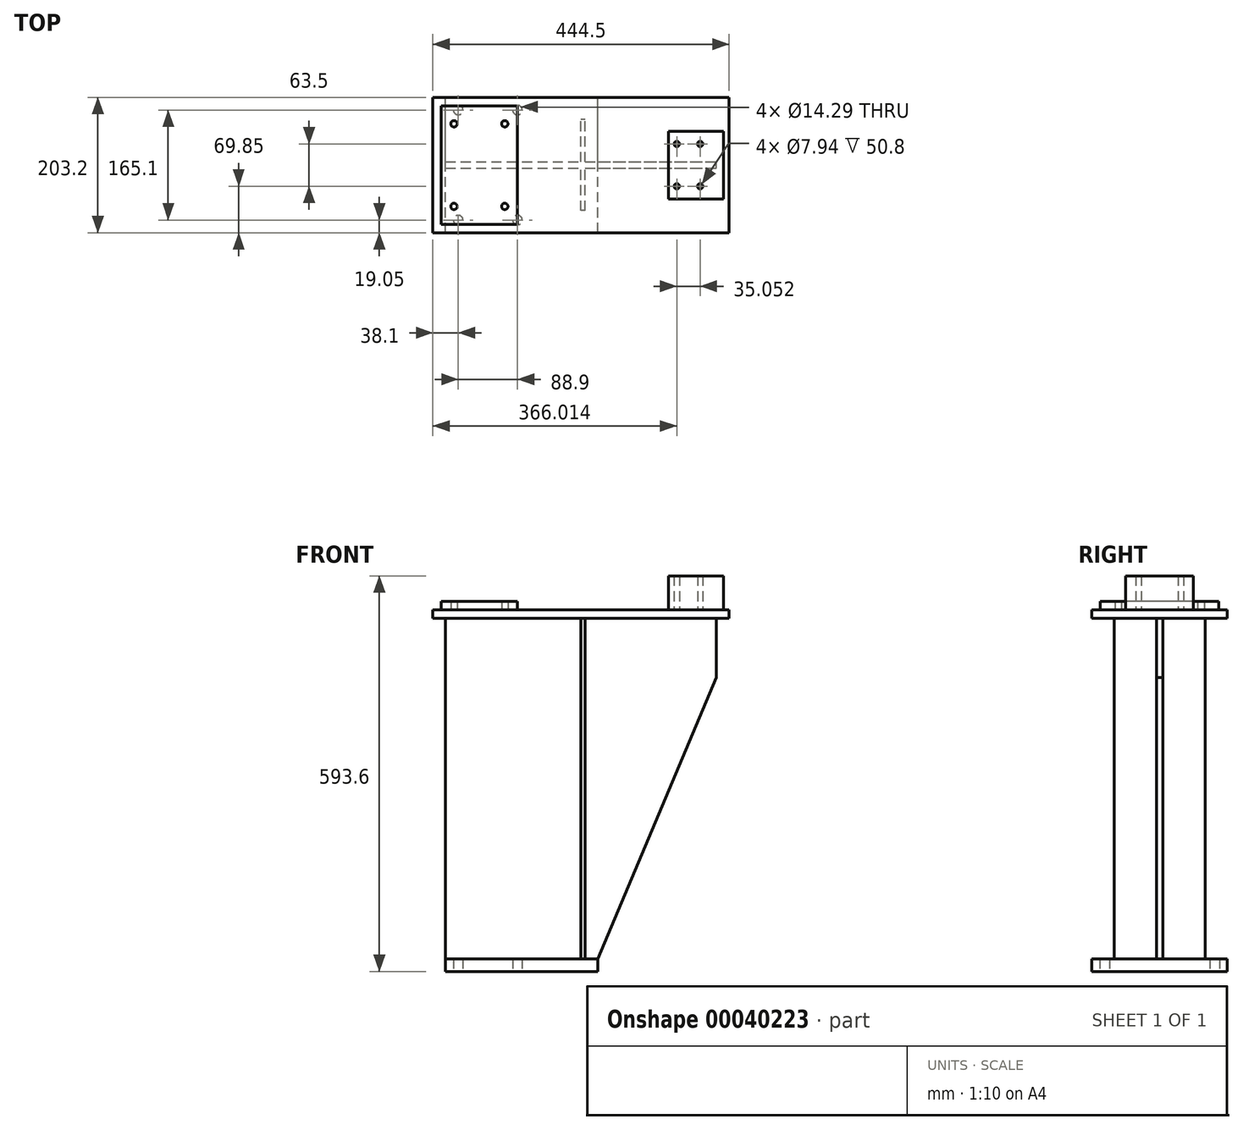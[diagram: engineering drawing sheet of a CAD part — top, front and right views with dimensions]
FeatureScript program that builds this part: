
annotation { "Feature Type Name" : "Feature", "Feature Type Description" : "" }
export const myFeature = defineFeature(function(context is Context, id is Id, definition is map)
    precondition{}
    {
        {
            var Q0;
            Q0=qCreatedBy(makeId("Top.planeOp"),FACE);
            var sketch = newSketch(context, id + "F0", { "sketchPlane" : qUnion([Q0])});
            skLineSegment(sketch, "E0.rect.bottom", {"start": v(-222.25, 101.6) * mm, "end": v(222.25, 101.6) * mm});
            skLineSegment(sketch, "E0.rect.top", {"start": v(-222.25, -101.6) * mm, "end": v(222.25, -101.6) * mm});
            skLineSegment(sketch, "E0.rect.left", {"start": v(-222.25, 101.6) * mm, "end": v(-222.25, -101.6) * mm});
            skLineSegment(sketch, "E0.rect.right", {"start": v(222.25, 101.6) * mm, "end": v(222.25, -101.6) * mm});
            skPoint(sketch, "E0.rect.middle", {"position": v(0, 0) * mm});
            skSolve(sketch);
        }
        {
            var Q0;
            Q0 = qSketchRegion(id + "F0", true);
            extrude(context, id + "F1", {"entities" : qUnion([Q0]), "oppositeDirection" : true, "depth" : 12.7 * mm});
        }
        {
            var Q0;
            Q0=qCreatedBy(makeId("Front.planeOp"),FACE);
            var sketch = newSketch(context, id + "F2", { "sketchPlane" : qUnion([Q0])});
            skLineSegment(sketch, "E1.0", {"start": v(-222.25, -12.7) * mm, "end": v(222.25, -12.7) * mm, "construction": true});
            skLineSegment(sketch, "E2", {"start": v(0, -12.7) * mm, "end": v(0, -523.75) * mm, "construction": true});
            skPoint(sketch, "E2.endSnap0", {"position": v(0, -12.7) * mm});
            skLineSegment(sketch, "E3.0", {"start": v(-203.2, -12.7) * mm, "end": v(-203.2, -523.75) * mm});
            skLineSegment(sketch, "E4.0", {"start": v(203.2, -12.7) * mm, "end": v(203.2, -101.6) * mm});
            skLineSegment(sketch, "E5", {"start": v(-203.2, -523.75) * mm, "end": v(25.4, -523.75) * mm});
            skLineSegment(sketch, "E6", {"start": v(203.2, -12.7) * mm, "end": v(-203.2, -12.7) * mm, "construction": true});
            skLineSegment(sketch, "E7.0", {"start": v(25.4, -12.7) * mm, "end": v(25.4, -523.75) * mm, "construction": true});
            skLineSegment(sketch, "E8.0", {"start": v(203.2, -101.6) * mm, "end": v(-203.2, -101.6) * mm, "construction": true});
            skLineSegment(sketch, "E9", {"start": v(25.4, -523.75) * mm, "end": v(203.2, -101.6) * mm});
            skLineSegment(sketch, "E10", {"start": v(-203.2, -12.7) * mm, "end": v(203.2, -12.7) * mm});
            skSolve(sketch);
        }
        {
            var Q0;
            Q0 = qSketchRegion(id + "F2", true);
            extrude(context, id + "F3", {"entities" : qUnion([Q0]), "operationType" : NewBodyOperationType.ADD, "endBound" : BoundingType.SYMMETRIC, "depth" : 9.65 * mm});
        }
        {
            var Q0;
            Q0=qCreatedBy(makeId("Front.planeOp"),FACE);
            var sketch = newSketch(context, id + "F4", { "sketchPlane" : qUnion([Q0])});
            skLineSegment(sketch, "E11", {"start": v(0, 171.52) * mm, "end": v(0, -557.34) * mm, "construction": true});
            skLineSegment(sketch, "E12.0", {"start": v(0, -12.7) * mm, "end": v(0, -523.75) * mm});
            skLineSegment(sketch, "E13.0", {"start": v(6.35, -12.7) * mm, "end": v(6.35, -523.75) * mm});
            skLineSegment(sketch, "E14", {"start": v(6.35, -12.7) * mm, "end": v(0, -12.7) * mm});
            skLineSegment(sketch, "E15", {"start": v(0, -523.75) * mm, "end": v(6.35, -523.75) * mm});
            skSolve(sketch);
        }
        {
            var Q0;
            Q0 = qSketchRegion(id + "F4", true);
            extrude(context, id + "F5", {"entities" : qUnion([Q0]), "operationType" : NewBodyOperationType.ADD, "endBound" : BoundingType.SYMMETRIC, "depth" : 136.53 * mm});
        }
        {
            var Q0;
            Q0=makeQuery(id+"F5.boolean.opBoolean","MERGE",FACE,{"derivedFrom":[makeQuery(id+"F3.opExtrude","SWEPT_FACE",FACE,{"disambiguationData":[OSD([sQuery(id+"F2.wireOp",EDGE,"E5")])]}),makeQuery(id+"F5.opExtrude","SWEPT_FACE",FACE,{"disambiguationData":[OSD([sQuery(id+"F4.wireOp",EDGE,"E15")])]})]});
            var sketch = newSketch(context, id + "F6", { "sketchPlane" : qUnion([Q0])});
            skLineSegment(sketch, "E16.0", {"start": v(-203.2, 101.6) * mm, "end": v(-203.2, -4.83) * mm});
            skLineSegment(sketch, "E17", {"start": v(0, 0) * mm, "end": v(-240.16, 0) * mm, "construction": true});
            skLineSegment(sketch, "E18.0", {"start": v(25.4, 101.6) * mm, "end": v(-203.2, 101.6) * mm});
            skPoint(sketch, "E19.orphan", {"position": v(-203.2, 4.83) * mm});
            skLineSegment(sketch, "E20.0", {"start": v(25.4, 101.6) * mm, "end": v(25.4, -4.83) * mm});
            skLineSegment(sketch, "E21.MirrorCS", {"start": v(-203.2, -101.6) * mm, "end": v(-203.2, 4.83) * mm});
            skLineSegment(sketch, "E22.MirrorCS", {"start": v(25.4, -101.6) * mm, "end": v(-203.2, -101.6) * mm});
            skLineSegment(sketch, "E23.MirrorCS", {"start": v(25.4, -101.6) * mm, "end": v(25.4, 4.83) * mm});
            skSolve(sketch);
        }
        {
            var Q0;
            Q0 = qSketchRegion(id + "F6", true);
            extrude(context, id + "F7", {"entities" : qUnion([Q0]), "operationType" : NewBodyOperationType.ADD, "depth" : 19.05 * mm});
        }
        {
            var Q0;
            Q0=makeQuery(id+"F7.opExtrude","CAP_FACE",FACE,{"disambiguationData":[OSD([sQuery(id+"F6.wireOp",EDGE,"E16.0"),sQuery(id+"F6.wireOp",EDGE,"E18.0"),sQuery(id+"F6.wireOp",EDGE,"E20.0"),sQuery(id+"F6.wireOp",EDGE,"E21.MirrorCS"),sQuery(id+"F6.wireOp",EDGE,"E22.MirrorCS"),sQuery(id+"F6.wireOp",EDGE,"E23.MirrorCS")])],"isStart":false});
            var sketch = newSketch(context, id + "F8", { "sketchPlane" : qUnion([Q0])});
            skLineSegment(sketch, "E24.0", {"start": v(-184.15, 101.6) * mm, "end": v(-184.15, -101.6) * mm, "construction": true});
            skLineSegment(sketch, "E25.0", {"start": v(-95.25, 101.6) * mm, "end": v(-95.25, -101.6) * mm, "construction": true});
            skLineSegment(sketch, "E26", {"start": v(-203.2, 0) * mm, "end": v(25.4, 0) * mm, "construction": true});
            skLineSegment(sketch, "E27.0", {"start": v(-203.2, 82.55) * mm, "end": v(25.4, 82.55) * mm, "construction": true});
            skPoint(sketch, "E28", {"position": v(-95.25, 82.55) * mm});
            skPoint(sketch, "E29", {"position": v(-184.15, 82.55) * mm});
            skPoint(sketch, "E30.MirrorP", {"position": v(-95.25, -82.55) * mm});
            skPoint(sketch, "E31.MirrorP", {"position": v(-184.15, -82.55) * mm});
            skSolve(sketch);
        }
        {
            var Q0;
            Q0=sQuery(id+"F8.wireOp",VERTEX,"E28");
            var Q1;
            Q1=sQuery(id+"F8.wireOp",VERTEX,"E29");
            var Q2;
            Q2=sQuery(id+"F8.wireOp",VERTEX,"E30.MirrorP");
            var Q3;
            Q3=sQuery(id+"F8.wireOp",VERTEX,"E31.MirrorP");
            var Q4;
            Q4=makeQuery(id+"F1.opExtrude","SWEPT_BODY",BODY,{"disambiguationData":[OSD([sQuery(id+"F0.wireOp",EDGE,"E0.rect.bottom"),sQuery(id+"F0.wireOp",EDGE,"E0.rect.top"),sQuery(id+"F0.wireOp",EDGE,"E0.rect.left"),sQuery(id+"F0.wireOp",EDGE,"E0.rect.right")])]});
            hole(context, id + "F9", {"style" : HoleStyle.SIMPLE, "holeDiameter" : 14.29 * mm, "endStyle" : HoleEndStyle.BLIND, "holeDepth" : 38.1 * mm, "locations" : qUnion([Q0, Q1, Q2, Q3]), "scope" : qUnion([Q4])});
        }
        {
            var Q0;
            Q0=makeQuery(id+"F1.opExtrude","CAP_FACE",FACE,{"disambiguationData":[OSD([sQuery(id+"F0.wireOp",EDGE,"E0.rect.bottom"),sQuery(id+"F0.wireOp",EDGE,"E0.rect.top"),sQuery(id+"F0.wireOp",EDGE,"E0.rect.left"),sQuery(id+"F0.wireOp",EDGE,"E0.rect.right")])],"isStart":true});
            var sketch = newSketch(context, id + "F10", { "sketchPlane" : qUnion([Q0])});
            skLineSegment(sketch, "E32", {"start": v(-222.25, 0) * mm, "end": v(222.25, 0) * mm, "construction": true});
            skLineSegment(sketch, "E33.0.0", {"start": v(222.25, 101.6) * mm, "end": v(-222.25, 101.6) * mm, "construction": true});
            skLineSegment(sketch, "E33.0.1", {"start": v(-222.25, 101.6) * mm, "end": v(-222.25, -101.6) * mm, "construction": true});
            skLineSegment(sketch, "E33.0.2", {"start": v(-222.25, -101.6) * mm, "end": v(222.25, -101.6) * mm, "construction": true});
            skLineSegment(sketch, "E33.0.3", {"start": v(222.25, -101.6) * mm, "end": v(222.25, 101.6) * mm, "construction": true});
            skLineSegment(sketch, "E34.0", {"start": v(-152.4, 101.6) * mm, "end": v(-152.4, -101.6) * mm, "construction": true});
            skLineSegment(sketch, "E35.0", {"start": v(-209.55, 88.9) * mm, "end": v(-209.55, -88.9) * mm});
            skLineSegment(sketch, "E36.0", {"start": v(-95.25, 88.9) * mm, "end": v(-95.25, -88.9) * mm});
            skLineSegment(sketch, "E37.0", {"start": v(-209.55, 88.9) * mm, "end": v(-95.25, 88.9) * mm});
            skLineSegment(sketch, "E38.0", {"start": v(-209.55, -88.9) * mm, "end": v(-95.25, -88.9) * mm});
            skLineSegment(sketch, "E39.0", {"start": v(-114.3, 101.6) * mm, "end": v(-114.3, -101.6) * mm, "construction": true});
            skLineSegment(sketch, "E40.0", {"start": v(-222.25, 61.98) * mm, "end": v(222.25, 61.98) * mm, "construction": true});
            skCircle(sketch, "E41", {"center": v(-114.3, 61.98) * mm, "radius": 4.83 * mm});
            skCircle(sketch, "E42.MirrorC", {"center": v(-190.5, 61.98) * mm, "radius": 4.83 * mm});
            skCircle(sketch, "E43.MirrorC", {"center": v(-190.5, -61.98) * mm, "radius": 4.83 * mm});
            skCircle(sketch, "E44.MirrorC", {"center": v(-114.3, -61.98) * mm, "radius": 4.83 * mm});
            skSolve(sketch);
        }
        {
            var Q0;
            Q0 = qSketchRegion(id + "F10", true);
            extrude(context, id + "F11", {"entities" : qUnion([Q0]), "operationType" : NewBodyOperationType.ADD, "depth" : 12.7 * mm});
        }
        {
            var Q0;
            Q0=makeQuery(id+"F10.imprint","IMPRINT",FACE,{"disambiguationData":[TD([[makeQuery(id+"F10.imprint","IMPRINT",EDGE,{"derivedFrom":sQuery(id+"F10.wireOp",EDGE,"E35.0")}),-1.0]])]});
            var sketch = newSketch(context, id + "F12", { "sketchPlane" : qUnion([Q0])});
            skLineSegment(sketch, "E45.0", {"start": v(131.06, 50.8) * mm, "end": v(131.06, -50.8) * mm});
            skLineSegment(sketch, "E46.0", {"start": v(213.61, 50.8) * mm, "end": v(213.61, -50.8) * mm});
            skLineSegment(sketch, "E47.0", {"start": v(131.06, 50.8) * mm, "end": v(213.61, 50.8) * mm});
            skLineSegment(sketch, "E48.0", {"start": v(131.06, -50.8) * mm, "end": v(213.61, -50.8) * mm});
            skLineSegment(sketch, "E49.0", {"start": v(143.76, 101.6) * mm, "end": v(143.76, -101.6) * mm, "construction": true});
            skLineSegment(sketch, "E50.0", {"start": v(178.82, 101.6) * mm, "end": v(178.82, -101.6) * mm, "construction": true});
            skLineSegment(sketch, "E51.0", {"start": v(-222.25, 31.75) * mm, "end": v(222.25, 31.75) * mm, "construction": true});
            skLineSegment(sketch, "E52.0", {"start": v(-222.25, -31.75) * mm, "end": v(222.25, -31.75) * mm, "construction": true});
            skCircle(sketch, "E53", {"center": v(143.76, 31.75) * mm, "radius": 3.97 * mm});
            skCircle(sketch, "E54", {"center": v(178.82, 31.75) * mm, "radius": 3.97 * mm});
            skCircle(sketch, "E55", {"center": v(178.82, -31.75) * mm, "radius": 3.97 * mm});
            skCircle(sketch, "E56", {"center": v(143.76, -31.75) * mm, "radius": 3.97 * mm});
            skSolve(sketch);
        }
        {
            var Q0;
            Q0 = qSketchRegion(id + "F12", true);
            extrude(context, id + "F13", {"entities" : qUnion([Q0]), "operationType" : NewBodyOperationType.ADD, "depth" : 50.8 * mm});
        }
    });
